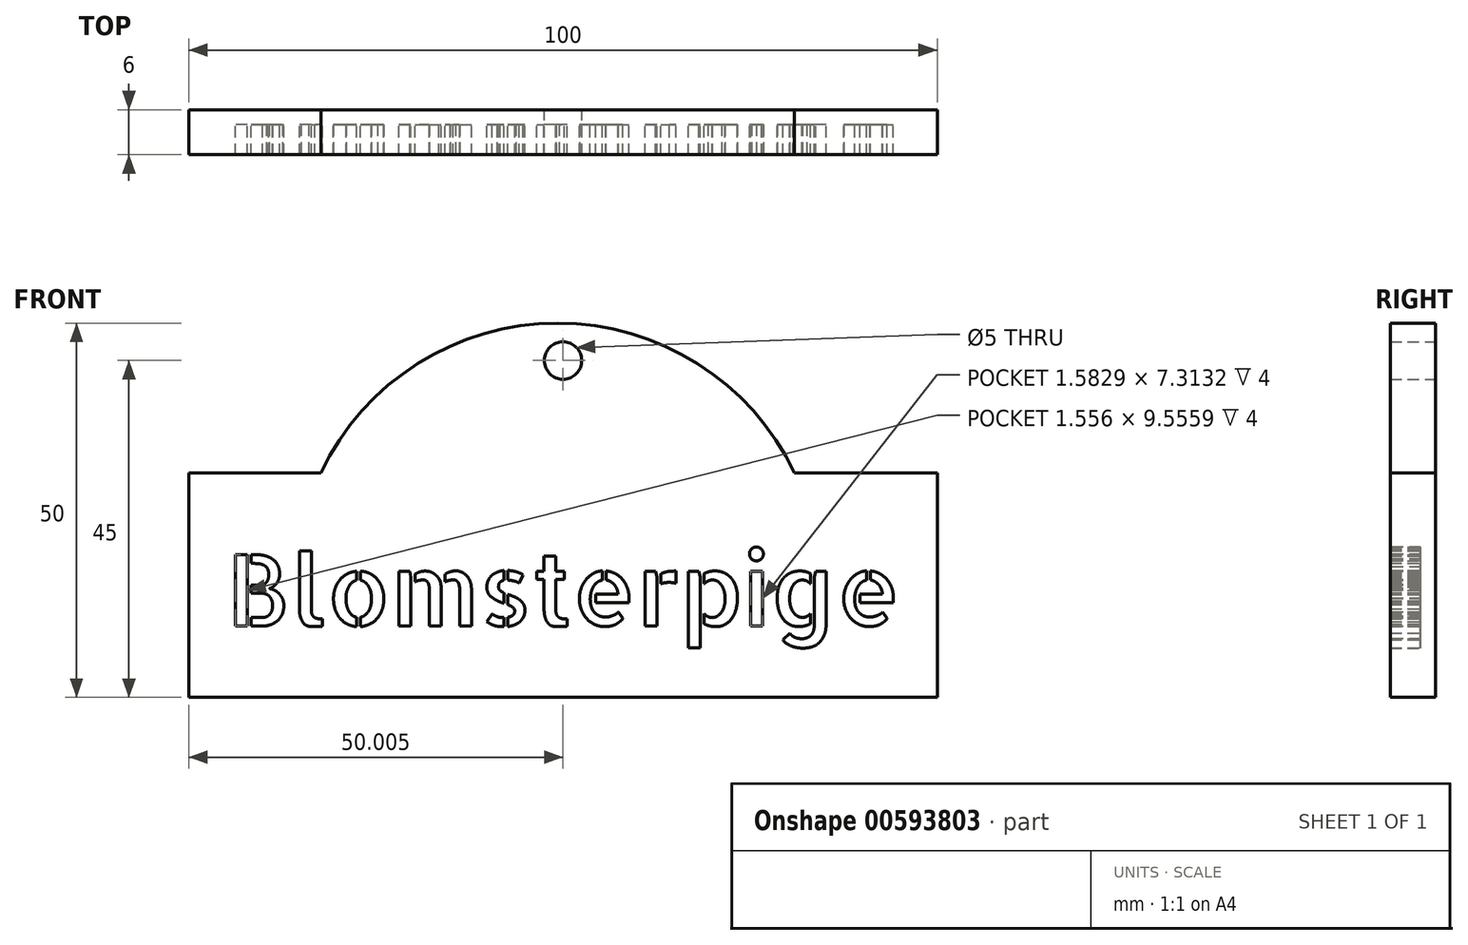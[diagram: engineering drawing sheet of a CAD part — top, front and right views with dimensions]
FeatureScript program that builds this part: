
annotation { "Feature Type Name" : "Feature", "Feature Type Description" : "" }
export const myFeature = defineFeature(function(context is Context, id is Id, definition is map)
    precondition{}
    {
        {
            var Q0;
            Q0=qCreatedBy(makeId("Front.planeOp"),FACE);
            var sketch = newSketch(context, id + "F0", { "sketchPlane" : qUnion([Q0])});
            skLineSegment(sketch, "E0.bottom", {"start": v(-53.18, 34.17) * mm, "end": v(-35.52, 34.17) * mm});
            skLineSegment(sketch, "E0.top", {"start": v(-53.18, 4.17) * mm, "end": v(46.82, 4.17) * mm});
            skLineSegment(sketch, "E0.left", {"start": v(-53.18, 34.17) * mm, "end": v(-53.18, 4.17) * mm});
            skLineSegment(sketch, "E0.right", {"start": v(46.82, 34.17) * mm, "end": v(46.82, 4.17) * mm});
            skArc(sketch, "E1", {"start": v(27.73, 34.17) * mm, "mid": v(-3.9, 54.17) * mm, "end": v(-35.52, 34.17) * mm});
            skCircle(sketch, "E2", {"center": v(-3.18, 49.17) * mm, "radius": 2.5 * mm});
            skText(sketch, "E3", { "text": "Blomsterpige", "fontName": "AllertaStencil-Regular.ttf"});
            skPoint(sketch, "E4", {"position": v(-3.18, 4.17) * mm});
            skPoint(sketch, "E5", {"position": v(46.82, 19.17) * mm});
            skPoint(sketch, "E6", {"position": v(41.82, 18.45) * mm});
            skLineSegment(sketch, "E7.trimOffspring", {"start": v(27.73, 34.17) * mm, "end": v(46.82, 34.17) * mm});
            const initialGuessF0  = {"E3": [-0.04818, 0.01367, 1, 0, 0.00956]};
            skSetInitialGuess(sketch, initialGuessF0);
            skSolve(sketch);
        }
        {
            var Q0;
            Q0=makeQuery(id+"F0.imprint","IMPRINT",FACE,{"disambiguationData":[TD([[makeQuery(id+"F0.imprint","IMPRINT",EDGE,{"derivedFrom":sQuery(id+"F0.wireOp",EDGE,"E3.sketch_text.stroke-152")}),-1.0]])]});
            var Q1;
            Q1=makeQuery(id+"F0.imprint","IMPRINT",FACE,{"disambiguationData":[TD([[makeQuery(id+"F0.imprint","IMPRINT",EDGE,{"derivedFrom":sQuery(id+"F0.wireOp",EDGE,"E3.sketch_text.stroke-161")}),-1.0]])]});
            var Q2;
            Q2=makeQuery(id+"F0.imprint","IMPRINT",FACE,{"disambiguationData":[TD([[makeQuery(id+"F0.imprint","IMPRINT",EDGE,{"derivedFrom":sQuery(id+"F0.wireOp",EDGE,"E3.sketch_text.stroke-320")}),-1.0]])]});
            var Q3;
            Q3=makeQuery(id+"F0.imprint","IMPRINT",FACE,{"disambiguationData":[TD([[makeQuery(id+"F0.imprint","IMPRINT",EDGE,{"derivedFrom":sQuery(id+"F0.wireOp",EDGE,"E3.sketch_text.stroke-146")}),-1.0]])]});
            var Q4;
            Q4=makeQuery(id+"F0.imprint","IMPRINT",FACE,{"disambiguationData":[TD([[makeQuery(id+"F0.imprint","IMPRINT",EDGE,{"derivedFrom":sQuery(id+"F0.wireOp",EDGE,"E3.sketch_text.stroke-132")}),-1.0]])]});
            var Q5;
            Q5=makeQuery(id+"F0.imprint","IMPRINT",FACE,{"disambiguationData":[TD([[makeQuery(id+"F0.imprint","IMPRINT",EDGE,{"derivedFrom":sQuery(id+"F0.wireOp",EDGE,"E3.sketch_text.stroke-114")}),-1.0]])]});
            var Q6;
            Q6=makeQuery(id+"F0.imprint","IMPRINT",FACE,{"disambiguationData":[TD([[makeQuery(id+"F0.imprint","IMPRINT",EDGE,{"derivedFrom":sQuery(id+"F0.wireOp",EDGE,"E3.sketch_text.stroke-98")}),-1.0]])]});
            var Q7;
            Q7=makeQuery(id+"F0.imprint","IMPRINT",FACE,{"disambiguationData":[TD([[makeQuery(id+"F0.imprint","IMPRINT",EDGE,{"derivedFrom":sQuery(id+"F0.wireOp",EDGE,"E3.sketch_text.stroke-93")}),-1.0]])]});
            var Q8;
            Q8 = qSketchRegion(id + "F0", true);
            var Q9;
            Q9=makeQuery(id+"F0.imprint","IMPRINT",FACE,{"disambiguationData":[TD([[makeQuery(id+"F0.imprint","IMPRINT",EDGE,{"derivedFrom":sQuery(id+"F0.wireOp",EDGE,"E3.sketch_text.stroke-77")}),-1.0]])]});
            var Q10;
            Q10=makeQuery(id+"F0.imprint","IMPRINT",FACE,{"disambiguationData":[TD([[makeQuery(id+"F0.imprint","IMPRINT",EDGE,{"derivedFrom":sQuery(id+"F0.wireOp",EDGE,"E3.sketch_text.stroke-61")}),-1.0]])]});
            var Q11;
            Q11=makeQuery(id+"F0.imprint","IMPRINT",FACE,{"disambiguationData":[TD([[makeQuery(id+"F0.imprint","IMPRINT",EDGE,{"derivedFrom":sQuery(id+"F0.wireOp",EDGE,"E3.sketch_text.stroke-43")}),-1.0]])]});
            var Q12;
            Q12=makeQuery(id+"F0.imprint","IMPRINT",FACE,{"disambiguationData":[TD([[makeQuery(id+"F0.imprint","IMPRINT",EDGE,{"derivedFrom":sQuery(id+"F0.wireOp",EDGE,"E3.sketch_text.stroke-39")}),-1.0]])]});
            var Q13;
            Q13=makeQuery(id+"F0.imprint","IMPRINT",FACE,{"disambiguationData":[TD([[makeQuery(id+"F0.imprint","IMPRINT",EDGE,{"derivedFrom":sQuery(id+"F0.wireOp",EDGE,"E3.sketch_text.stroke-0")}),-1.0]])]});
            var Q14;
            Q14=makeQuery(id+"F0.imprint","IMPRINT",FACE,{"disambiguationData":[TD([[makeQuery(id+"F0.imprint","IMPRINT",EDGE,{"derivedFrom":sQuery(id+"F0.wireOp",EDGE,"E3.sketch_text.stroke-200")}),-1.0]])]});
            var Q15;
            Q15=makeQuery(id+"F0.imprint","IMPRINT",FACE,{"disambiguationData":[TD([[makeQuery(id+"F0.imprint","IMPRINT",EDGE,{"derivedFrom":sQuery(id+"F0.wireOp",EDGE,"E3.sketch_text.stroke-175")}),-1.0]])]});
            var Q16;
            Q16=makeQuery(id+"F0.imprint","IMPRINT",FACE,{"disambiguationData":[TD([[makeQuery(id+"F0.imprint","IMPRINT",EDGE,{"derivedFrom":sQuery(id+"F0.wireOp",EDGE,"E3.sketch_text.stroke-213")}),-1.0]])]});
            var Q17;
            Q17=makeQuery(id+"F0.imprint","IMPRINT",FACE,{"disambiguationData":[TD([[makeQuery(id+"F0.imprint","IMPRINT",EDGE,{"derivedFrom":sQuery(id+"F0.wireOp",EDGE,"E3.sketch_text.stroke-294")}),-1.0]])]});
            var Q18;
            Q18=makeQuery(id+"F0.imprint","IMPRINT",FACE,{"disambiguationData":[TD([[makeQuery(id+"F0.imprint","IMPRINT",EDGE,{"derivedFrom":sQuery(id+"F0.wireOp",EDGE,"E3.sketch_text.stroke-286")}),-1.0]])]});
            var Q19;
            Q19=makeQuery(id+"F0.imprint","IMPRINT",FACE,{"disambiguationData":[TD([[makeQuery(id+"F0.imprint","IMPRINT",EDGE,{"derivedFrom":sQuery(id+"F0.wireOp",EDGE,"E3.sketch_text.stroke-282")}),-1.0]])]});
            var Q20;
            Q20=makeQuery(id+"F0.imprint","IMPRINT",FACE,{"disambiguationData":[TD([[makeQuery(id+"F0.imprint","IMPRINT",EDGE,{"derivedFrom":sQuery(id+"F0.wireOp",EDGE,"E3.sketch_text.stroke-256")}),-1.0]])]});
            var Q21;
            Q21=makeQuery(id+"F0.imprint","IMPRINT",FACE,{"disambiguationData":[TD([[makeQuery(id+"F0.imprint","IMPRINT",EDGE,{"derivedFrom":sQuery(id+"F0.wireOp",EDGE,"E3.sketch_text.stroke-251")}),-1.0]])]});
            var Q22;
            Q22=makeQuery(id+"F0.imprint","IMPRINT",FACE,{"disambiguationData":[TD([[makeQuery(id+"F0.imprint","IMPRINT",EDGE,{"derivedFrom":sQuery(id+"F0.wireOp",EDGE,"E3.sketch_text.stroke-244")}),-1.0]])]});
            var Q23;
            Q23=makeQuery(id+"F0.imprint","IMPRINT",FACE,{"disambiguationData":[TD([[makeQuery(id+"F0.imprint","IMPRINT",EDGE,{"derivedFrom":sQuery(id+"F0.wireOp",EDGE,"E3.sketch_text.stroke-237")}),-1.0]])]});
            var Q24;
            Q24=makeQuery(id+"F0.imprint","IMPRINT",FACE,{"disambiguationData":[TD([[makeQuery(id+"F0.imprint","IMPRINT",EDGE,{"derivedFrom":sQuery(id+"F0.wireOp",EDGE,"E3.sketch_text.stroke-337")}),-1.0]])]});
            var Q25;
            Q25=makeQuery(id+"F0.imprint","IMPRINT",FACE,{"disambiguationData":[TD([[makeQuery(id+"F0.imprint","IMPRINT",EDGE,{"derivedFrom":sQuery(id+"F0.wireOp",EDGE,"E3.sketch_text.stroke-350")}),-1.0]])]});
            var Q26;
            Q26=makeQuery(id+"F0.imprint","IMPRINT",FACE,{"disambiguationData":[TD([[makeQuery(id+"F0.imprint","IMPRINT",EDGE,{"derivedFrom":sQuery(id+"F0.wireOp",EDGE,"E0.bottom")}),-1.0]])]});
            extrude(context, id + "F1", {"entities" : qUnion([Q0, Q1, Q2, Q3, Q4, Q5, Q6, Q7, Q8, Q9, Q10, Q11, Q12, Q13, Q14, Q15, Q16, Q17, Q18, Q19, Q20, Q21, Q22, Q23, Q24, Q25, Q26]), "depth" : 2 * mm, "offsetDistance" : 25 * mm});
        }
        {
            var Q0;
            Q0=makeQuery(id+"F0.imprint","IMPRINT",FACE,{"disambiguationData":[TD([[makeQuery(id+"F0.imprint","IMPRINT",EDGE,{"derivedFrom":sQuery(id+"F0.wireOp",EDGE,"E0.bottom")}),-1.0]])]});
            extrude(context, id + "F2", {"entities" : qUnion([Q0]), "operationType" : NewBodyOperationType.ADD, "depth" : 6 * mm, "offsetDistance" : 25 * mm});
        }
    });
